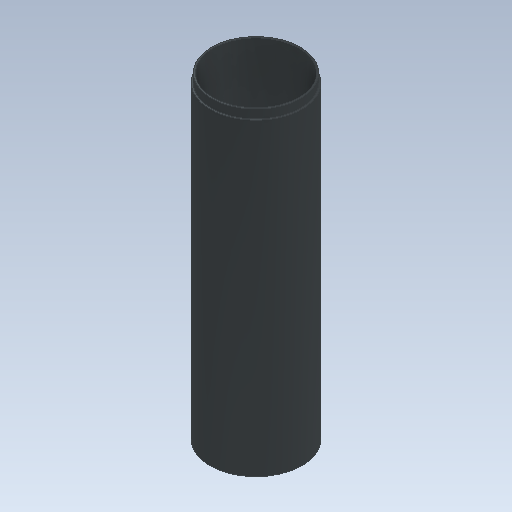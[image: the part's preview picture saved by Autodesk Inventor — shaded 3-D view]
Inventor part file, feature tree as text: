
AUTODESK INVENTOR PART (.ipt)
format: ipt  version: 2020.3 (Build 243373000, 373)  size: 136,704 bytes
history: native  units: mm
features: extrude x2, sketch x1
ambient origin geometry x8: Origin, YZ Plane, XZ Plane, XY Plane, X Axis, Y Axis, Z Axis, Center Point
bodies: Solid1 (feature_tree)
feature tree (3):
  sketch  "Sketch1"  dims[d0=51.8mm d1=50.0mm d2=53.6mm d3=95.0mm d4=0.0mm d5=180.0mm d6=0.0mm d10=85.0mm d11=0.0mm]
  extrude  "Extrusion1"  Depth=85.0mm
  extrude  "Extrusion2"  Depth=85.0mm
